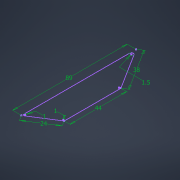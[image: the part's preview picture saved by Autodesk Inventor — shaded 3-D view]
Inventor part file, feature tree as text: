
AUTODESK INVENTOR PART (.ipt)
format: ipt  version: 2022 (Build 260153000, 153)  size: 105,984 bytes
history: native  units: mm
features: sketch x2
ambient origin geometry x8: Origin, YZ Plane, XZ Plane, XY Plane, X Axis, Y Axis, Z Axis, Center Point
feature tree (2):
  sketch  "Sketch1"  dims[d0=89.0mm]
  sketch  "Sketch2"  dims[d1=38.0mm d2=44.0mm d3=24.0mm d4=38.0mm d5=5.0mm d6=7.0mm d7=15.0mm d8=38.0mm d9=5.0mm d10=1.0mm d11=1.0mm d12=1.0mm d13=0.5mm d14=89.0mm d15=38.0mm d16=44.0mm d17=24.0mm d25=1.0mm d26=1.0mm d27=1.5mm]
